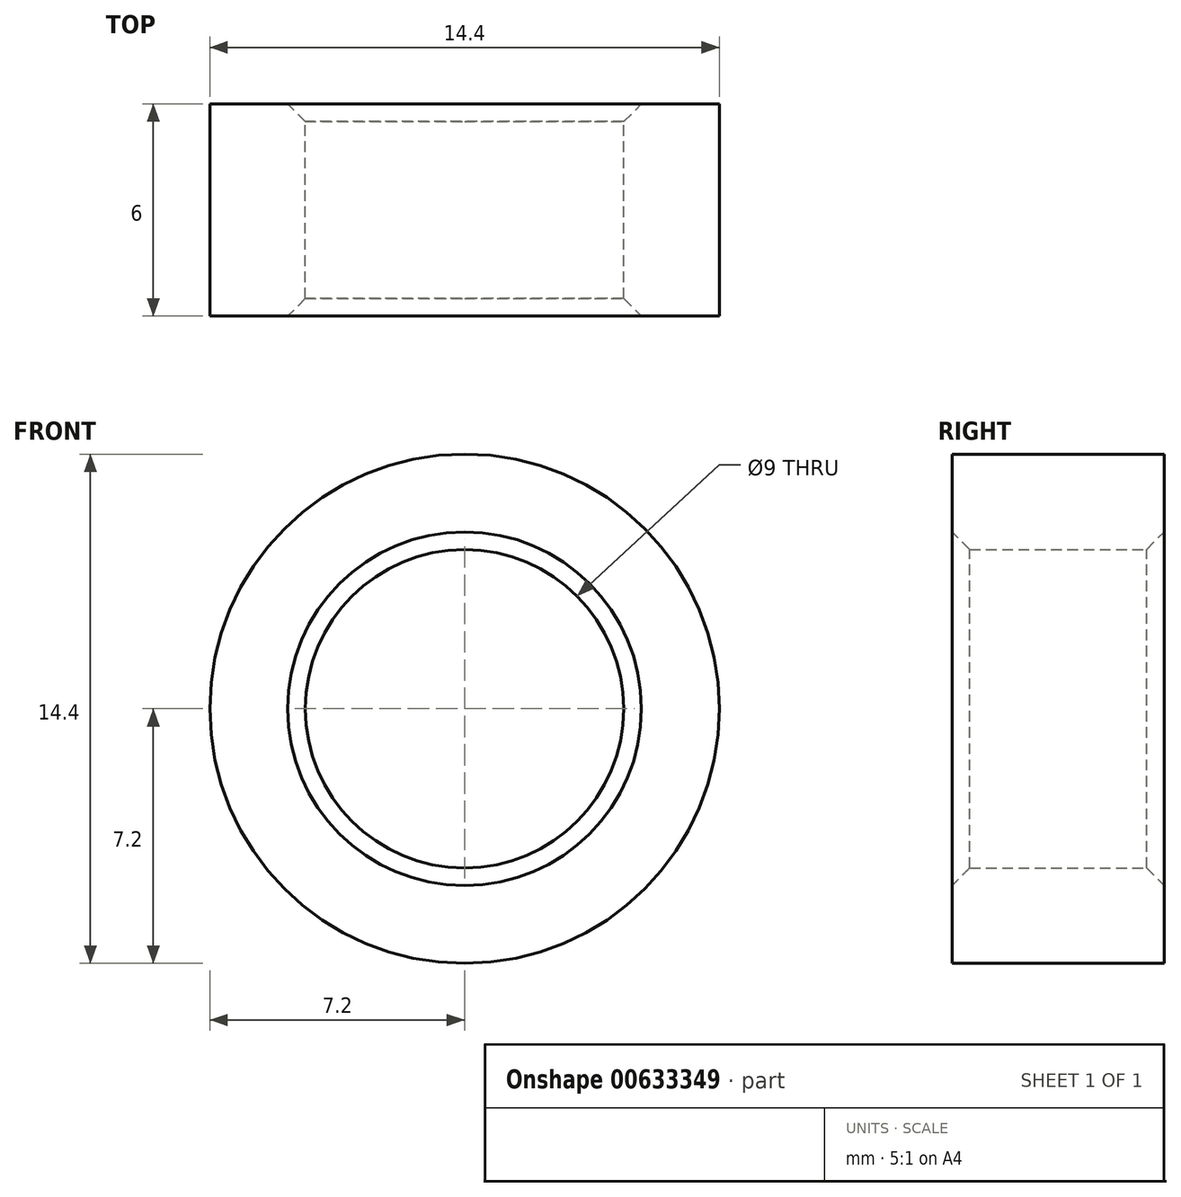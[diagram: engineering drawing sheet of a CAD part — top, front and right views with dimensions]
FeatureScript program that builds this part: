
annotation { "Feature Type Name" : "Feature", "Feature Type Description" : "" }
export const myFeature = defineFeature(function(context is Context, id is Id, definition is map)
    precondition{}
    {
        {
            var Q0;
            Q0=qCreatedBy(makeId("Front.planeOp"),FACE);
            var sketch = newSketch(context, id + "F0", { "sketchPlane" : qUnion([Q0])});
            skCircle(sketch, "E0", {"center": v(0, 0) * mm, "radius": 7.2 * mm});
            skCircle(sketch, "E1", {"center": v(0, 0) * mm, "radius": 4.5 * mm});
            skSolve(sketch);
        }
        {
            var Q0;
            Q0=makeQuery(id+"F0.imprint","IMPRINT",FACE,{"disambiguationData":[TD([[makeQuery(id+"F0.imprint","IMPRINT",EDGE,{"derivedFrom":sQuery(id+"F0.wireOp",EDGE,"E0")}),1.0]])]});
            extrude(context, id + "F1", {"entities" : qUnion([Q0]), "depth" : 6 * mm, "offsetDistance" : 25 * mm});
        }
        {
            var Q0;
            Q0=makeQuery(id+"F1.opExtrude","CAP_EDGE",EDGE,{"disambiguationData":[OSD([sQuery(id+"F0.wireOp",EDGE,"E1")])],"isStart":false});
            var Q1;
            Q1=makeQuery(id+"F1.opExtrude","CAP_EDGE",EDGE,{"disambiguationData":[OSD([sQuery(id+"F0.wireOp",EDGE,"E1")])],"isStart":true});
            chamfer(context, id + "F2", {"entities" : qUnion([Q0, Q1]), "width" : 0.5 * mm, "tangentPropagation" : true});
        }
    });
